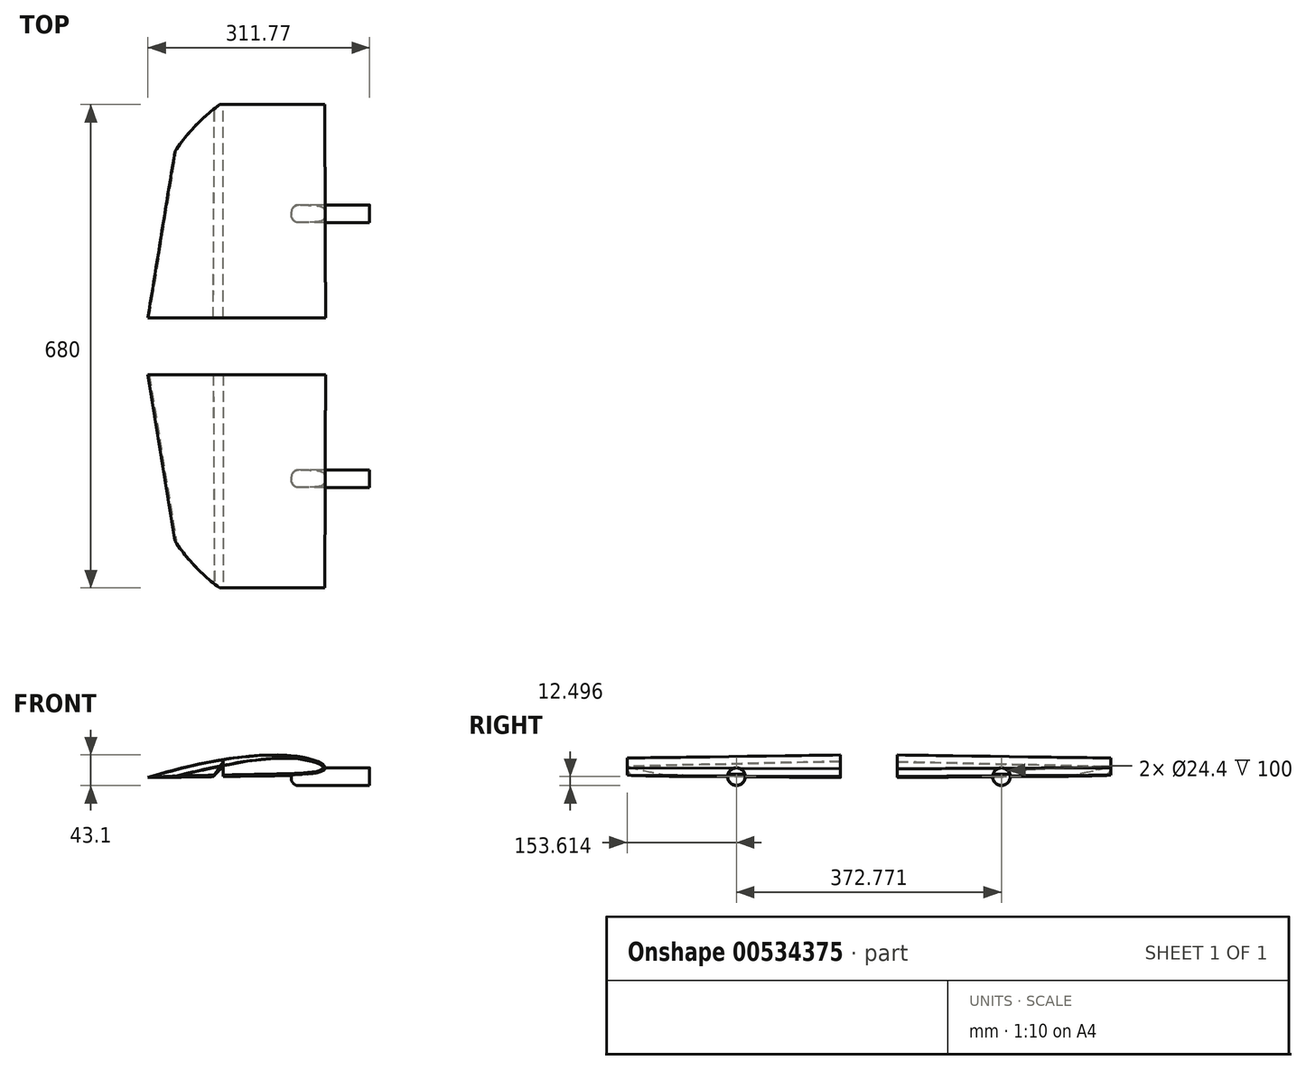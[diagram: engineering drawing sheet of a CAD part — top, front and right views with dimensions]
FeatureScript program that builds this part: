
annotation { "Feature Type Name" : "Feature", "Feature Type Description" : "" }
export const myFeature = defineFeature(function(context is Context, id is Id, definition is map)
    precondition{}
    {
        {
            var Q0;
            Q0=qCreatedBy(makeId("Front.planeOp"),FACE);
            var sketch = newSketch(context, id + "F0", { "sketchPlane" : qUnion([Q0])});
            skFitSpline(sketch, "E0.0.0", {"points": [v(128.23, 37.15) * mm, v(128.28, 37.44) * mm, v(128.28, 38.04) * mm, v(128.05, 38.94) * mm, v(127.62, 39.8) * mm, v(127.03, 40.64) * mm, v(126.33, 41.42) * mm, v(125.54, 42.16) * mm, v(124.7, 42.86) * mm, v(123.52, 43.74) * mm, v(121.98, 44.75) * mm, v(120.1, 45.83) * mm, v(118.53, 46.62) * mm, v(117.3, 47.2) * mm, v(116.38, 47.59) * mm, v(115.47, 47.96) * mm, v(114.57, 48.31) * mm, v(113.66, 48.64) * mm, v(112.75, 48.96) * mm, v(111.84, 49.27) * mm, v(110.6, 49.67) * mm, v(109, 50.17) * mm, v(107.06, 50.76) * mm, v(105.09, 51.33) * mm, v(103.1, 51.88) * mm, v(101.1, 52.4) * mm, v(99.12, 52.87) * mm, v(97.15, 53.31) * mm, v(95.18, 53.71) * mm, v(93.2, 54.08) * mm, v(91.23, 54.41) * mm, v(88.57, 54.83) * mm, v(85.22, 55.28) * mm, v(81.18, 55.73) * mm, v(77.14, 56.06) * mm, v(73.1, 56.3) * mm, v(69.07, 56.46) * mm, v(65.02, 56.57) * mm, v(59.62, 56.64) * mm, v(54.22, 56.62) * mm, v(48.82, 56.5) * mm, v(44.78, 56.38) * mm, v(40.73, 56.22) * mm, v(36.7, 56.02) * mm, v(32.65, 55.78) * mm, v(27.27, 55.4) * mm, v(20.55, 54.85) * mm, v(13.83, 54.19) * mm, v(8.47, 53.59) * mm, v(4.45, 53.1) * mm, v(0.43, 52.59) * mm, v(-4.92, 51.86) * mm, v(-11.6, 50.88) * mm, v(-18.25, 49.8) * mm, v(-23.57, 48.9) * mm, v(-27.55, 48.18) * mm, v(-31.53, 47.44) * mm, v(-36.82, 46.43) * mm, v(-43.4, 45.1) * mm, v(-49.97, 43.7) * mm, v(-55.24, 42.54) * mm, v(-59.19, 41.65) * mm, v(-63.13, 40.73) * mm, v(-67.06, 39.8) * mm, v(-70.98, 38.86) * mm, v(-74.25, 38.05) * mm, v(-76.87, 37.4) * mm, v(-79.49, 36.74) * mm, v(-84.07, 35.57) * mm, v(-88.66, 34.37) * mm, v(-92.57, 33.32) * mm, v(-94.53, 32.8) * mm, v(-96.48, 32.26) * mm, v(-98.44, 31.73) * mm, v(-100.42, 31.18) * mm, v(-102.4, 30.63) * mm, v(-104.36, 30.08) * mm, v(-106.3, 29.53) * mm, v(-108.25, 28.97) * mm, v(-110.2, 28.41) * mm, v(-112.13, 27.84) * mm, v(-114.7, 27.08) * mm, v(-117.91, 26.1) * mm, v(-120.48, 25.29) * mm, v(-121.77, 24.87) * mm]});
            skFitSpline(sketch, "E0.0.1", {"points": [v(-121.77, 24.87) * mm, v(-120.44, 24.86) * mm, v(-117.77, 24.85) * mm, v(-113.77, 24.85) * mm, v(-109.82, 24.88) * mm, v(-105.88, 24.93) * mm, v(-101.92, 24.98) * mm, v(-97.92, 25.04) * mm, v(-93.93, 25.1) * mm, v(-89.93, 25.16) * mm, v(-86.6, 25.21) * mm, v(-83.93, 25.25) * mm, v(-81.93, 25.28) * mm, v(-79.94, 25.31) * mm, v(-77.97, 25.34) * mm, v(-76.05, 25.37) * mm, v(-74.17, 25.4) * mm, v(-72.34, 25.43) * mm, v(-69.94, 25.46) * mm, v(-67.55, 25.5) * mm, v(-65.12, 25.54) * mm, v(-63.26, 25.56) * mm, v(-61.35, 25.6) * mm, v(-59.4, 25.62) * mm, v(-57.74, 25.64) * mm, v(-56.4, 25.66) * mm, v(-55.07, 25.68) * mm, v(-53.4, 25.7) * mm, v(-50.74, 25.74) * mm, v(-47.41, 25.8) * mm, v(-43.41, 25.85) * mm, v(-40.08, 25.9) * mm, v(-37.42, 25.94) * mm, v(-35.42, 25.97) * mm, v(-33.42, 26) * mm, v(-31.42, 26.02) * mm, v(-29.42, 26.05) * mm, v(-27.47, 26.08) * mm, v(-25.57, 26.1) * mm, v(-23.73, 26.14) * mm, v(-21.95, 26.16) * mm, v(-19.62, 26.2) * mm, v(-17.32, 26.23) * mm, v(-14.96, 26.27) * mm, v(-13.15, 26.3) * mm, v(-11.27, 26.32) * mm, v(-9.34, 26.35) * mm, v(-7.69, 26.37) * mm, v(-6.35, 26.39) * mm, v(-5.02, 26.4) * mm, v(-3.36, 26.43) * mm, v(-0.7, 26.47) * mm, v(2.64, 26.52) * mm, v(6.64, 26.58) * mm, v(11.97, 26.66) * mm, v(18.63, 26.75) * mm, v(26.63, 26.86) * mm, v(34.62, 26.98) * mm, v(42.62, 27.1) * mm, v(50.61, 27.2) * mm, v(57.27, 27.3) * mm, v(62.6, 27.39) * mm, v(66.6, 27.46) * mm, v(70.6, 27.53) * mm, v(74.59, 27.62) * mm, v(77.9, 27.7) * mm, v(80.57, 27.79) * mm, v(82.58, 27.86) * mm, v(84.58, 27.93) * mm, v(86.59, 28.01) * mm, v(88.58, 28.1) * mm, v(90.57, 28.18) * mm, v(92.55, 28.27) * mm, v(94.53, 28.37) * mm, v(96.52, 28.5) * mm, v(98.52, 28.63) * mm, v(100.54, 28.8) * mm, v(102.56, 28.98) * mm, v(104.59, 29.17) * mm, v(106.6, 29.37) * mm, v(108.57, 29.57) * mm, v(110.5, 29.75) * mm, v(112.4, 29.94) * mm, v(114.3, 30.16) * mm, v(115.92, 30.41) * mm, v(117.24, 30.67) * mm, v(118.58, 30.97) * mm, v(120.29, 31.43) * mm, v(122.33, 32.13) * mm, v(123.99, 32.86) * mm, v(125.23, 33.55) * mm, v(126.1, 34.13) * mm, v(126.88, 34.78) * mm, v(127.53, 35.5) * mm, v(128.01, 36.3) * mm, v(128.19, 36.86) * mm, v(128.23, 37.15) * mm]});
            skLineSegment(sketch, "E1", {"start": v(-15.83, 26.25) * mm, "end": v(-15.83, 46.77) * mm});
            skLineSegment(sketch, "E2", {"start": v(-15.83, 46.77) * mm, "end": v(-29.65, 26.05) * mm});
            skSolve(sketch);
        }
        {
            var Q0;
            Q0=qCreatedBy(makeId("Front.planeOp"),FACE);
            cPlane(context, id + "F1", {"entities" : qUnion([Q0]), "cplaneType" : CPlaneType.OFFSET, "offset" : 300 * mm, "width" : 150 * mm, "height" : 150 * mm});
        }
        {
            var Q0;
            Q0=qCreatedBy(id+"F1.planeOp",FACE);
            var sketch = newSketch(context, id + "F2", { "sketchPlane" : qUnion([Q0])});
            skFitSpline(sketch, "E3.0.0", {"points": [v(127.87, 35.85) * mm, v(127.9, 36.15) * mm, v(127.88, 36.74) * mm, v(127.6, 37.63) * mm, v(127.12, 38.48) * mm, v(126.5, 39.28) * mm, v(125.75, 40.03) * mm, v(124.93, 40.73) * mm, v(124.05, 41.38) * mm, v(122.83, 42.2) * mm, v(121.24, 43.13) * mm, v(119.3, 44.12) * mm, v(117.7, 44.83) * mm, v(116.43, 45.34) * mm, v(115.5, 45.69) * mm, v(114.57, 46.01) * mm, v(113.65, 46.32) * mm, v(112.73, 46.6) * mm, v(111.8, 46.88) * mm, v(110.87, 47.14) * mm, v(109.6, 47.48) * mm, v(108, 47.9) * mm, v(106.02, 48.39) * mm, v(104.02, 48.86) * mm, v(102, 49.3) * mm, v(99.99, 49.72) * mm, v(97.98, 50.1) * mm, v(95.99, 50.44) * mm, v(94, 50.74) * mm, v(92, 51) * mm, v(90, 51.24) * mm, v(87.33, 51.52) * mm, v(83.96, 51.8) * mm, v(79.9, 52.05) * mm, v(75.85, 52.18) * mm, v(71.8, 52.21) * mm, v(67.75, 52.17) * mm, v(63.7, 52.07) * mm, v(58.3, 51.87) * mm, v(52.9, 51.57) * mm, v(47.52, 51.2) * mm, v(43.48, 50.87) * mm, v(39.44, 50.5) * mm, v(35.41, 50.1) * mm, v(31.39, 49.65) * mm, v(26.02, 49) * mm, v(19.33, 48.11) * mm, v(12.66, 47.1) * mm, v(7.32, 46.24) * mm, v(3.33, 45.55) * mm, v(-0.66, 44.84) * mm, v(-5.97, 43.84) * mm, v(-12.6, 42.52) * mm, v(-19.2, 41.11) * mm, v(-24.46, 39.93) * mm, v(-28.41, 39.02) * mm, v(-32.35, 38.08) * mm, v(-37.59, 36.8) * mm, v(-44.1, 35.14) * mm, v(-50.6, 33.41) * mm, v(-55.8, 31.98) * mm, v(-59.7, 30.9) * mm, v(-63.6, 29.78) * mm, v(-67.48, 28.65) * mm, v(-71.35, 27.5) * mm, v(-74.58, 26.54) * mm, v(-77.17, 25.75) * mm, v(-79.75, 24.96) * mm, v(-84.27, 23.56) * mm, v(-88.8, 22.13) * mm, v(-92.66, 20.89) * mm, v(-94.58, 20.26) * mm, v(-96.5, 19.63) * mm, v(-98.45, 19) * mm, v(-100.4, 18.35) * mm, v(-102.34, 17.7) * mm, v(-104.27, 17.05) * mm, v(-106.2, 16.4) * mm, v(-108.11, 15.75) * mm, v(-110.03, 15.09) * mm, v(-111.93, 14.42) * mm, v(-114.46, 13.53) * mm, v(-117.62, 12.38) * mm, v(-120.15, 11.44) * mm, v(-121.42, 10.97) * mm]});
            skFitSpline(sketch, "E3.0.1", {"points": [v(-122.73, 26.21) * mm, v(-121.4, 26.2) * mm, v(-118.72, 26.2) * mm, v(-114.72, 26.23) * mm, v(-110.76, 26.28) * mm, v(-106.83, 26.34) * mm, v(-102.86, 26.42) * mm, v(-98.86, 26.5) * mm, v(-94.86, 26.58) * mm, v(-90.86, 26.66) * mm, v(-87.53, 26.72) * mm, v(-84.86, 26.78) * mm, v(-82.86, 26.82) * mm, v(-80.86, 26.86) * mm, v(-78.9, 26.9) * mm, v(-76.97, 26.94) * mm, v(-75.1, 26.98) * mm, v(-73.26, 27.01) * mm, v(-70.85, 27.06) * mm, v(-68.47, 27.1) * mm, v(-66.03, 27.16) * mm, v(-64.17, 27.2) * mm, v(-62.26, 27.23) * mm, v(-60.3, 27.27) * mm, v(-58.64, 27.3) * mm, v(-57.3, 27.33) * mm, v(-55.98, 27.35) * mm, v(-54.3, 27.38) * mm, v(-51.64, 27.44) * mm, v(-48.3, 27.5) * mm, v(-44.3, 27.58) * mm, v(-40.97, 27.64) * mm, v(-38.3, 27.7) * mm, v(-36.3, 27.73) * mm, v(-34.3, 27.77) * mm, v(-32.3, 27.81) * mm, v(-30.3, 27.85) * mm, v(-28.35, 27.89) * mm, v(-26.45, 27.93) * mm, v(-24.6, 27.96) * mm, v(-22.82, 28) * mm, v(-20.49, 28.04) * mm, v(-18.19, 28.09) * mm, v(-15.83, 28.13) * mm, v(-14.01, 28.17) * mm, v(-12.14, 28.2) * mm, v(-10.2, 28.24) * mm, v(-8.55, 28.28) * mm, v(-7.22, 28.3) * mm, v(-5.88, 28.33) * mm, v(-4.22, 28.36) * mm, v(-1.55, 28.41) * mm, v(1.78, 28.48) * mm, v(5.79, 28.55) * mm, v(11.12, 28.66) * mm, v(17.79, 28.79) * mm, v(25.79, 28.94) * mm, v(33.79, 29.1) * mm, v(41.8, 29.25) * mm, v(49.8, 29.4) * mm, v(56.46, 29.53) * mm, v(61.8, 29.64) * mm, v(65.8, 29.73) * mm, v(69.8, 29.83) * mm, v(73.79, 29.93) * mm, v(77.1, 30.03) * mm, v(79.78, 30.13) * mm, v(81.78, 30.21) * mm, v(83.8, 30.3) * mm, v(85.8, 30.39) * mm, v(87.8, 30.48) * mm, v(89.79, 30.58) * mm, v(91.77, 30.68) * mm, v(93.75, 30.79) * mm, v(95.74, 30.91) * mm, v(97.74, 31.06) * mm, v(99.76, 31.24) * mm, v(101.78, 31.43) * mm, v(103.8, 31.64) * mm, v(105.81, 31.85) * mm, v(107.79, 32.05) * mm, v(109.72, 32.25) * mm, v(111.63, 32.44) * mm, v(113.53, 32.68) * mm, v(115.15, 32.94) * mm, v(116.47, 33.2) * mm, v(117.8, 33.5) * mm, v(119.51, 33.97) * mm, v(121.56, 34.69) * mm, v(123.2, 35.43) * mm, v(124.45, 36.12) * mm, v(125.31, 36.7) * mm, v(126.1, 37.36) * mm, v(126.74, 38.08) * mm, v(127.22, 38.88) * mm, v(127.39, 39.45) * mm, v(127.43, 39.74) * mm]});
            skLineSegment(sketch, "E4", {"start": v(-15.82, 28.13) * mm, "end": v(-15.82, 40.03) * mm});
            skLineSegment(sketch, "E5", {"start": v(-15.82, 40.03) * mm, "end": v(-28.06, 27.9) * mm});
            skSolve(sketch);
        }
        {
            var Q0;
            Q0=makeQuery(id+"F0.imprint","IMPRINT",FACE,{"disambiguationData":[TD([[makeQuery(id+"F0.imprint","IMPRINT",EDGE,{"derivedFrom":sQuery(id+"F0.wireOp",EDGE,"E0.0.0")}),1.0]])]});
            var Q1;
            Q1=makeQuery(id+"F2.imprint","IMPRINT",FACE,{"disambiguationData":[TD([[makeQuery(id+"F2.imprint","IMPRINT",EDGE,{"derivedFrom":sQuery(id+"F2.wireOp",EDGE,"E3.0.0")}),1.0]])]});
            loft(context, id + "F3", {"sheetProfilesArray" : [{ "sheetProfileEntities" : qUnion([Q0]) }, { "sheetProfileEntities" : qUnion([Q1]) }]});
        }
        {
            var Q0;
            Q0=qCreatedBy(makeId("Front.planeOp"),FACE);
            cPlane(context, id + "F4", {"entities" : qUnion([Q0]), "cplaneType" : CPlaneType.OFFSET, "offset" : 40 * mm, "oppositeDirection" : true, "width" : 150 * mm, "height" : 150 * mm});
        }
        {
            var Q0;
            Q0=makeQuery(id+"F3.opLoft","SWEPT_BODY",BODY,{"disambiguationData":[OSD([makeQuery(id+"F0.imprint","IMPRINT",FACE,{"disambiguationData":[TD([[makeQuery(id+"F0.imprint","IMPRINT",EDGE,{"derivedFrom":sQuery(id+"F0.wireOp",EDGE,"E0.0.0")}),1.0]])]}),makeQuery(id+"F2.imprint","IMPRINT",FACE,{"disambiguationData":[TD([[makeQuery(id+"F2.imprint","IMPRINT",EDGE,{"derivedFrom":sQuery(id+"F2.wireOp",EDGE,"E3.0.0")}),1.0]])]})])]});
            var Q1;
            Q1=qCreatedBy(id+"F4.planeOp",FACE);
            mirror(context, id + "F5", {"entities" : qUnion([Q0]), "mirrorPlane" : qUnion([Q1])});
        }
        {
            var Q0;
            Q0=qCreatedBy(makeId("Right.planeOp"),FACE);
            cPlane(context, id + "F6", {"entities" : qUnion([Q0]), "cplaneType" : CPlaneType.OFFSET, "offset" : 80 * mm, "width" : 150 * mm, "height" : 150 * mm});
        }
        {
            var Q0;
            Q0=qCreatedBy(id+"F6.planeOp",FACE);
            var sketch = newSketch(context, id + "F7", { "sketchPlane" : qUnion([Q0])});
            skCircle(sketch, "E6", {"center": v(-146.39, 26.05) * mm, "radius": 12.5 * mm});
            skCircle(sketch, "E7.MirrorC", {"center": v(226.39, 26.05) * mm, "radius": 12.5 * mm});
            skSolve(sketch);
        }
        {
            var Q0;
            Q0=qSketchRegion(id+"F7",true);
            extrude(context, id + "F8", {"entities" : qUnion([Q0]), "operationType" : NewBodyOperationType.ADD, "depth" : 110 * mm, "offsetDistance" : 25 * mm});
        }
        {
            var Q0;
            Q0=makeQuery(id+"F8.opExtrude","CAP_EDGE",EDGE,{"disambiguationData":[OSD([sQuery(id+"F7.wireOp",EDGE,"E6")])],"isStart":true});
            var Q1;
            Q1=makeQuery(id+"F8.opExtrude","CAP_EDGE",EDGE,{"disambiguationData":[OSD([sQuery(id+"F7.wireOp",EDGE,"E7.MirrorC")])],"isStart":true});
            fillet(context, id + "F9", {"entities" : qUnion([Q0, Q1]), "radius" : 10 * mm, "tangentPropagation" : true, "allowEdgeOverflow" : false});
        }
        {
            var Q0;
            {var subQ2=sQuery(id+"F2.wireOp",EDGE,"E3.0.0");Q0=makeQuery(id+"F3.opLoft","CAP_FACE",FACE,{"disambiguationData":[OSD([makeQuery(id+"F2.imprint","IMPRINT",FACE,{"disambiguationData":[TD([[makeQuery(id+"F2.imprint","IMPRINT",EDGE,{"derivedFrom":subQ2}),1.0]])]})])],"isStart":true});}
            var Q1;
            {var subQ2=sQuery(id+"F2.wireOp",EDGE,"E3.0.0");Q1=makeQuery(id+"F5.opPattern","COPY",FACE,{"derivedFrom":makeQuery(id+"F3.opLoft","CAP_FACE",FACE,{"disambiguationData":[OSD([makeQuery(id+"F2.imprint","IMPRINT",FACE,{"disambiguationData":[TD([[makeQuery(id+"F2.imprint","IMPRINT",EDGE,{"derivedFrom":subQ2}),1.0]])]})])],"isStart":true}),"instanceName":"1"});}
            var Q2;
            Q2=makeQuery(id+"F8.opExtrude","CAP_FACE",FACE,{"disambiguationData":[OSD([sQuery(id+"F7.wireOp",EDGE,"E7.MirrorC")])],"isStart":false});
            var Q3;
            Q3=makeQuery(id+"F8.opExtrude","CAP_FACE",FACE,{"disambiguationData":[OSD([sQuery(id+"F7.wireOp",EDGE,"E6")])],"isStart":false});
            shell(context, id + "F10", {"entities" : qUnion([Q0, Q1, Q2, Q3]), "thickness" : .3 * mm});
        }
        {
            var Q0;
            Q0=qCreatedBy(makeId("Top.planeOp"),FACE);
            var sketch = newSketch(context, id + "F11", { "sketchPlane" : qUnion([Q0])});
            skLineSegment(sketch, "E8", {"start": v(-86.82, 309.23) * mm, "end": v(-73.01, 383.16) * mm});
            skLineSegment(sketch, "E9", {"start": v(-73.01, 383.16) * mm, "end": v(-16.27, 383.16) * mm});
            skArc(sketch, "E10.MirrorCS", {"start": v(-16.27, -303.16) * mm, "mid": v(-55.27, -269.75) * mm, "end": v(-86.82, -229.23) * mm});
            skLineSegment(sketch, "E11.MirrorCS", {"start": v(-86.82, -229.23) * mm, "end": v(-73.01, -303.16) * mm});
            skLineSegment(sketch, "E12.MirrorCS", {"start": v(-73.01, -303.16) * mm, "end": v(-16.27, -303.16) * mm});
            skArc(sketch, "E13.MirrorCS", {"start": v(-16.27, 383.16) * mm, "mid": v(-55.27, 349.75) * mm, "end": v(-86.82, 309.23) * mm});
            skSolve(sketch);
        }
        {
            var Q0;
            Q0 = qSketchRegion(id + "F11", true);
            extrude(context, id + "F12", {"entities" : qUnion([Q0]), "operationType" : NewBodyOperationType.REMOVE, "depth" : 70 * mm, "offsetDistance" : 25 * mm});
        }
    });
